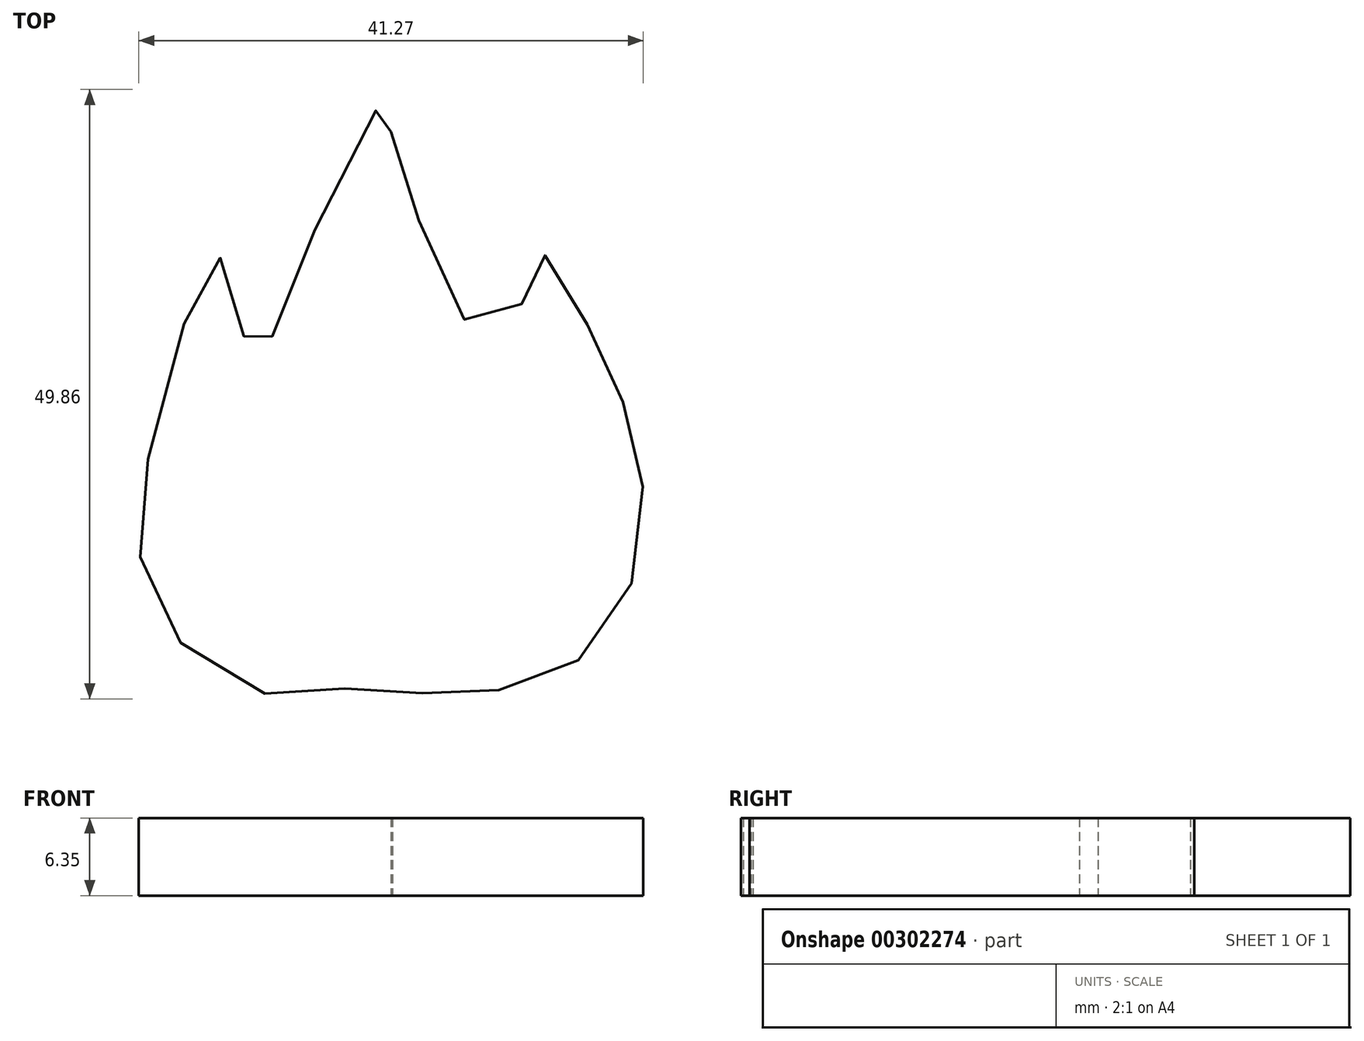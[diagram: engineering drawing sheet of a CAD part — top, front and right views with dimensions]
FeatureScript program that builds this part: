
annotation { "Feature Type Name" : "Feature", "Feature Type Description" : "" }
export const myFeature = defineFeature(function(context is Context, id is Id, definition is map)
    precondition{}
    {
        {
            var Q0;
            Q0=qCreatedBy(makeId("Top.planeOp"),FACE);
            var sketch = newSketch(context, id + "F0", { "sketchPlane" : qUnion([Q0])});
            skLineSegment(sketch, "E0.bottom", {"start": v(-37.56, 38.86) * mm, "end": v(38.64, 38.86) * mm});
            skLineSegment(sketch, "E0.top", {"start": v(-37.56, -37.34) * mm, "end": v(38.64, -37.34) * mm});
            skLineSegment(sketch, "E0.left", {"start": v(-37.56, 38.86) * mm, "end": v(-37.56, -37.34) * mm});
            skLineSegment(sketch, "E0.right", {"start": v(38.64, 38.86) * mm, "end": v(38.64, -37.34) * mm});
            skPoint(sketch, "E1.1.internal.snap0", {"position": v(-0.48, -33.61) * mm});
            skPoint(sketch, "E1.17.internal.snap0", {"position": v(-0.48, -33.61) * mm});
            skPoint(sketch, "E1.18.internal.snap0", {"position": v(-0.48, -33.61) * mm});
            skFitSpline(sketch, "E1", {"points": [v(-4.24, -30.1) * mm, v(-0.48, -30.92) * mm, v(4.16, -29.97) * mm, v(7.83, -30.21) * mm, v(12.27, -29.32) * mm, v(16.77, -25.95) * mm, v(19.5, -20.5) * mm, v(20.14, -14.05) * mm, v(19.37, -9.08) * mm, v(17.4, -4.08) * mm, v(15.43, 0) * mm, v(13.53, 3.25) * mm, v(11.17, 6.17) * mm, v(10.39, 1.9) * mm, v(7.25, -1.68) * mm, v(3.66, 4.37) * mm, v(1, 9.9) * mm, v(-0.48, 15.81) * mm, v(-0.48, 18.93) * mm, v(-3.92, 12.99) * mm, v(-8.63, 3.04) * mm, v(-10.8, -2.76) * mm, v(-11.26, -3.22) * mm, v(-12.64, -0.97) * mm, v(-14.26, 3.36) * mm, v(-14.66, 5.84) * mm, v(-18.12, -2.41) * mm, v(-20.72, -13.5) * mm, v(-20.98, -19.44) * mm, v(-18.77, -24.97) * mm, v(-13.6, -29.48) * mm, v(-8.17, -30.68) * mm, v(-4.24, -30.1) * mm]});
            skSolve(sketch);
        }
        {
            var Q0;
            Q0=makeQuery(id+"F0.imprint","IMPRINT",FACE,{"disambiguationData":[TD([[makeQuery(id+"F0.imprint","IMPRINT",EDGE,{"derivedFrom":sQuery(id+"F0.wireOp",EDGE,"E1")}),1.0]])]});
            extrude(context, id + "F1", {"entities" : qUnion([Q0]), "depth" : 6.35 * mm});
        }
    });
